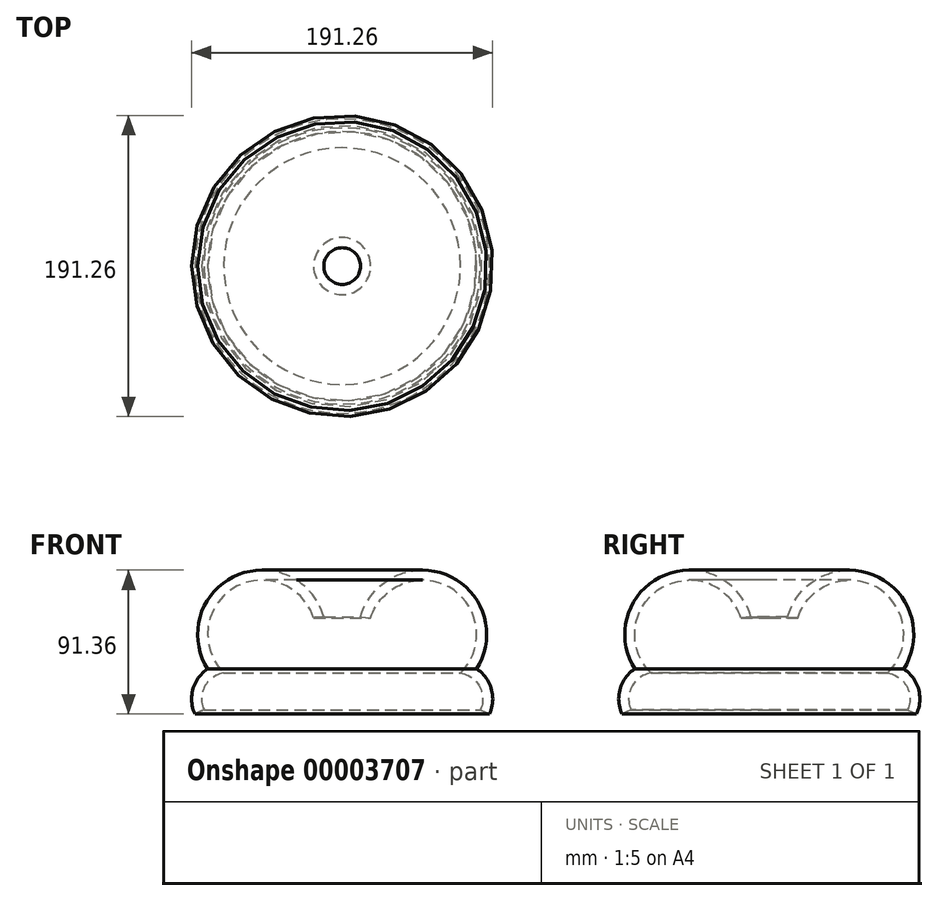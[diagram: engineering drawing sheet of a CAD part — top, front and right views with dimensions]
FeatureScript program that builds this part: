
annotation { "Feature Type Name" : "Feature", "Feature Type Description" : "" }
export const myFeature = defineFeature(function(context is Context, id is Id, definition is map)
    precondition{}
    {
        {
            var Q0;
            Q0=qCreatedBy(makeId("Front.planeOp"),FACE);
            var sketch = newSketch(context, id + "F0", { "sketchPlane" : qUnion([Q0])});
            skLineSegment(sketch, "E0", {"start": v(0, 0) * mm, "end": v(0, 116.57) * mm});
            skSolve(sketch);
        }
        {
            var Q0;
            Q0=qCreatedBy(makeId("Front.planeOp"),FACE);
            var sketch = newSketch(context, id + "F1", { "sketchPlane" : qUnion([Q0])});
            skArc(sketch, "E1", {"start": v(75.19, 96.33) * mm, "mid": v(69.07, 150.25) * mm, "end": v(18.14, 131.51) * mm});
            skArc(sketch, "E2", {"start": v(87.75, 73.04) * mm, "mid": v(87.3, 87.83) * mm, "end": v(75.19, 96.33) * mm});
            skArc(sketch, "E3.0", {"start": v(85.46, 99) * mm, "mid": v(67.6, 158.2) * mm, "end": v(11.64, 131.94) * mm});
            skArc(sketch, "E3.1", {"start": v(93.52, 70.37) * mm, "mid": v(94.78, 86.18) * mm, "end": v(85.46, 99) * mm});
            skLineSegment(sketch, "E4", {"start": v(11.64, 131.94) * mm, "end": v(18.14, 131.51) * mm});
            skLineSegment(sketch, "E5", {"start": v(87.75, 73.04) * mm, "end": v(93.52, 70.37) * mm});
            skSolve(sketch);
        }
        {
            var Q0;
            Q0=makeQuery(id+"F1.imprint","IMPRINT",FACE,{"disambiguationData":[TD([[makeQuery(id+"F1.imprint","IMPRINT",EDGE,{"derivedFrom":sQuery(id+"F1.wireOp",EDGE,"E1")}),-1.0]])]});
            var Q1;
            Q1=sQuery(id+"F0.wireOp",EDGE,"E0");
            revolve(context, id + "F2", {"entities" : qUnion([Q0]), "axis" : qUnion([Q1]), "revolveType" : RevolveType.FULL});
        }
    });
